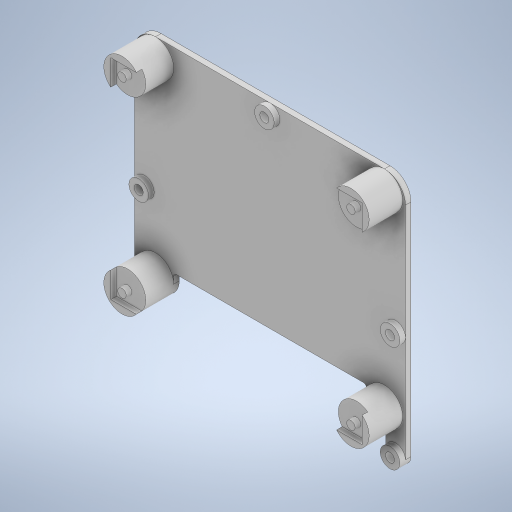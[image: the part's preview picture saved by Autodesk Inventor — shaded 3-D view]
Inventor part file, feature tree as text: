
AUTODESK INVENTOR PART (.ipt)
format: ipt  version: 2023 (Build 270158000, 158)  size: 382,464 bytes
history: native  units: mm
features: sketch x9, extrude x7, fillet x3, hole x1
ambient origin geometry x8: Origin, YZ Plane, XZ Plane, XY Plane, X Axis, Y Axis, Z Axis, Center Point
bodies: Volumenkörper1 (feature_tree)
feature tree (20):
  extrude  "Extrusion1"  Depth=97.0mm
  extrude  "Extrusion2"  Depth=2.0mm
  extrude  "Extrusion3"  Depth=13.0mm
  extrude  "Extrusion4"  Depth=75.0mm
  sketch  "Skizze9"  dims[d20=3.2mm d21=6.0mm d22=4.0mm d23=2.0mm d24=90.0deg d25=8.0mm d26=20.594885mm d28=2.0mm d29=0.0mm d30=31.5mm d31=7.0mm d33=2.0mm d34=0.0mm]
  extrude  "Extrusion7"  Depth=2.0mm TaperAngle=0.0deg
  extrude  "Extrusion6"  Depth=2.0mm TaperAngle=0.0deg
  hole  "Bohrung1"  [1 undecoded]
  extrude  "Extrusion5"  Depth=2.0mm TaperAngle=0.0deg
  fillet  "Rundung1"  Radius=31.5mm
  fillet  "Rundung2"  Radius=7.0mm
  fillet  "Rundung3"  Radius=2.0mm
  sketch  "Skizze10"  dims[d35=7.5mm d36=1.0mm d37=45.0mm d39=10.0mm d40=69.0mm d41=2.0mm d42=0.0mm d43=2.0mm d44=0.0mm d45=7.0mm d47=0.0mm d48=6.5mm d49=6.5mm]
  sketch  "Skizze1"  dims[d1=80.0mm d2=97.0mm]
  sketch  "Skizze2"  dims[d3=2.0mm d4=0.0mm d5=82.0mm]
  sketch  "Skizze3"  dims[d6=67.0mm d7=13.0mm]
  sketch  "Skizze4"  dims[d8=12.0mm d9=0.0mm d10=75.0mm]
  sketch  "Skizze5"  dims[d11=90.0mm d12=2.0mm d13=0.0mm]
  sketch  "Skizze6"  dims[d15=3.0mm d16=2.0mm d17=0.0mm]
  sketch  "Skizze7"  dims[d18=90.0mm d19=38.0mm]
note: 1 required parameter value undecoded (feature->parameter linkage not recoverable at this tier; creation-order binding heuristic only, values carry confidence <= 0.55)
